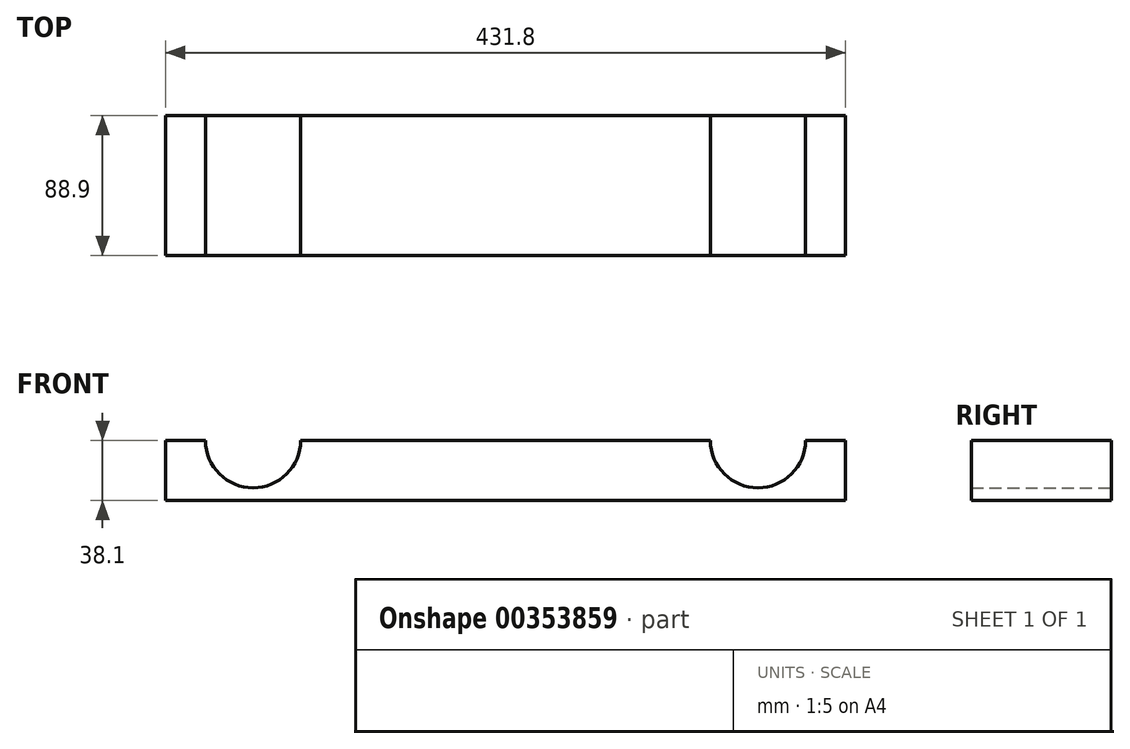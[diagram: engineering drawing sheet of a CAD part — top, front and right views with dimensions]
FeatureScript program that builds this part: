
annotation { "Feature Type Name" : "Feature", "Feature Type Description" : "" }
export const myFeature = defineFeature(function(context is Context, id is Id, definition is map)
    precondition{}
    {
        {
            var Q0;
            Q0=qCreatedBy(makeId("Front.planeOp"),FACE);
            var sketch = newSketch(context, id + "F0", { "sketchPlane" : qUnion([Q0])});
            skLineSegment(sketch, "E0.bottom", {"start": v(-181.74, 44) * mm, "end": v(-156.34, 44) * mm});
            skLineSegment(sketch, "E0.top", {"start": v(-181.74, 5.9) * mm, "end": v(250.06, 5.9) * mm});
            skLineSegment(sketch, "E0.left", {"start": v(-181.74, 44) * mm, "end": v(-181.74, 5.9) * mm});
            skLineSegment(sketch, "E0.right", {"start": v(250.06, 44) * mm, "end": v(250.06, 5.9) * mm});
            skLineSegment(sketch, "E1.0", {"start": v(194.5, 13.84) * mm, "end": v(194.5, 5.9) * mm, "construction": true});
            skArc(sketch, "E2", {"start": v(-156.34, 44) * mm, "mid": v(-126.18, 13.84) * mm, "end": v(-96.02, 44) * mm});
            skArc(sketch, "E3", {"start": v(164.33, 44) * mm, "mid": v(194.5, 13.84) * mm, "end": v(224.66, 44) * mm});
            skLineSegment(sketch, "E4.trimOffspring", {"start": v(-96.02, 44) * mm, "end": v(164.33, 44) * mm});
            skLineSegment(sketch, "E5.trimOffspring", {"start": v(224.66, 44) * mm, "end": v(250.06, 44) * mm});
            skSolve(sketch);
        }
        {
            var Q0;
            Q0=makeQuery(id+"F0.imprint","IMPRINT",FACE,{"disambiguationData":[TD([[makeQuery(id+"F0.imprint","IMPRINT",EDGE,{"derivedFrom":sQuery(id+"F0.wireOp",EDGE,"E0.bottom")}),-1.0]])]});
            extrude(context, id + "F1", {"entities" : qUnion([Q0]), "depth" : 88.9 * mm});
        }
    });
